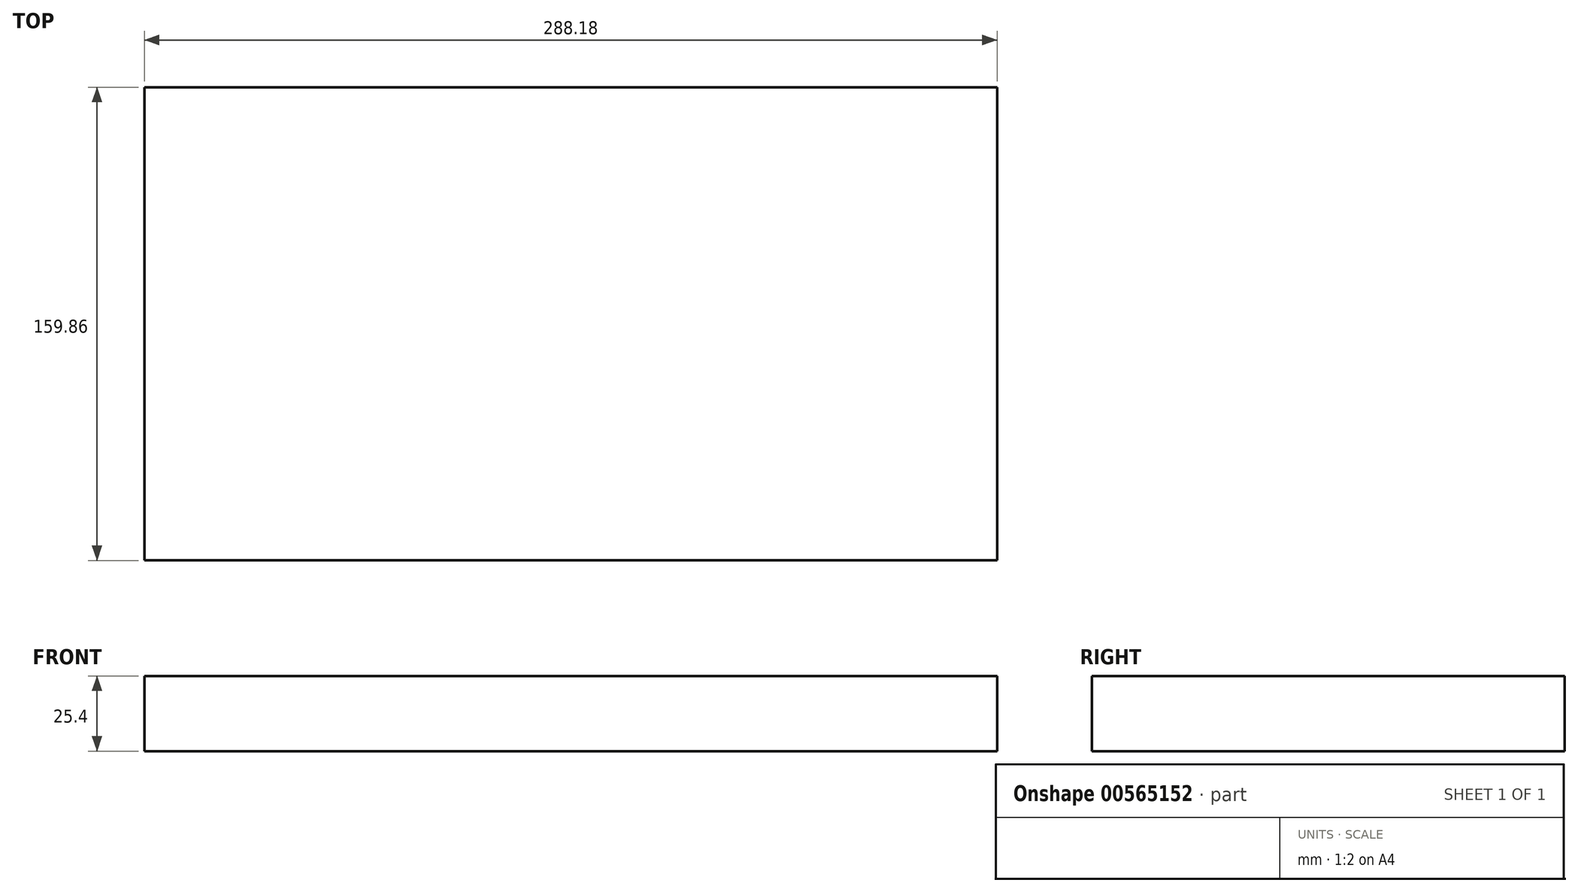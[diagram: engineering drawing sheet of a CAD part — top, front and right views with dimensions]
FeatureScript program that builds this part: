
annotation { "Feature Type Name" : "Feature", "Feature Type Description" : "" }
export const myFeature = defineFeature(function(context is Context, id is Id, definition is map)
    precondition{}
    {
        {
            var Q0;
            Q0=qCreatedBy(makeId("Top.planeOp"),FACE);
            var sketch = newSketch(context, id + "F0", { "sketchPlane" : qUnion([Q0])});
            skLineSegment(sketch, "E0.bottom", {"start": v(144.1, -79.93) * mm, "end": v(-144.1, -79.93) * mm});
            skLineSegment(sketch, "E0.top", {"start": v(144.1, 79.93) * mm, "end": v(-144.1, 79.93) * mm});
            skLineSegment(sketch, "E0.left", {"start": v(144.1, -79.93) * mm, "end": v(144.1, 79.93) * mm});
            skLineSegment(sketch, "E0.right", {"start": v(-144.1, -79.93) * mm, "end": v(-144.1, 79.93) * mm});
            skPoint(sketch, "E0.middle", {"position": v(0, 0) * mm});
            skSolve(sketch);
        }
        {
            var Q0;
            Q0 = qSketchRegion(id + "F0", true);
            extrude(context, id + "F1", {"entities" : qUnion([Q0]), "depth" : 25.4 * mm, "offsetDistance" : 25.4 * mm});
        }
    });
